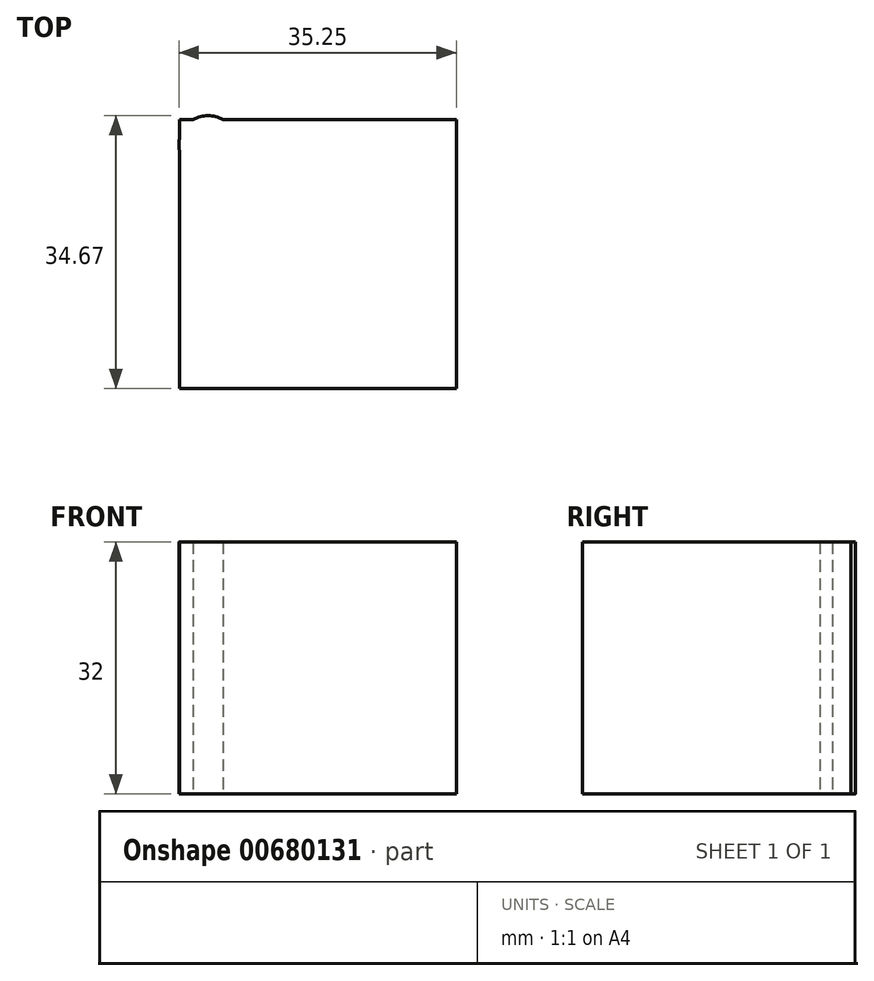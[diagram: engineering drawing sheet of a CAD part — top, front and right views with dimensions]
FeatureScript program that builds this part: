
annotation { "Feature Type Name" : "Feature", "Feature Type Description" : "" }
export const myFeature = defineFeature(function(context is Context, id is Id, definition is map)
    precondition{}
    {
        {
            var Q0;
            Q0=qCreatedBy(makeId("Top.planeOp"),FACE);
            var sketch = newSketch(context, id + "F0", { "sketchPlane" : qUnion([Q0])});
            skLineSegment(sketch, "E0.bottom", {"start": v(0, 0) * mm, "end": v(35.16, 0) * mm});
            skLineSegment(sketch, "E0.top", {"start": v(0, 34.15) * mm, "end": v(35.16, 34.15) * mm});
            skLineSegment(sketch, "E0.left", {"start": v(0, 0) * mm, "end": v(0, 34.15) * mm});
            skLineSegment(sketch, "E0.right", {"start": v(35.16, 0) * mm, "end": v(35.16, 34.15) * mm});
            skCircle(sketch, "E1", {"center": v(3.62, 30.96) * mm, "radius": 3.7 * mm});
            skSolve(sketch);
        }
        {
            var Q0;
            Q0 = qSketchRegion(id + "F0", true);
            extrude(context, id + "F1", {"entities" : qUnion([Q0]), "depth" : 32 * mm, "offsetDistance" : 25 * mm});
        }
    });
